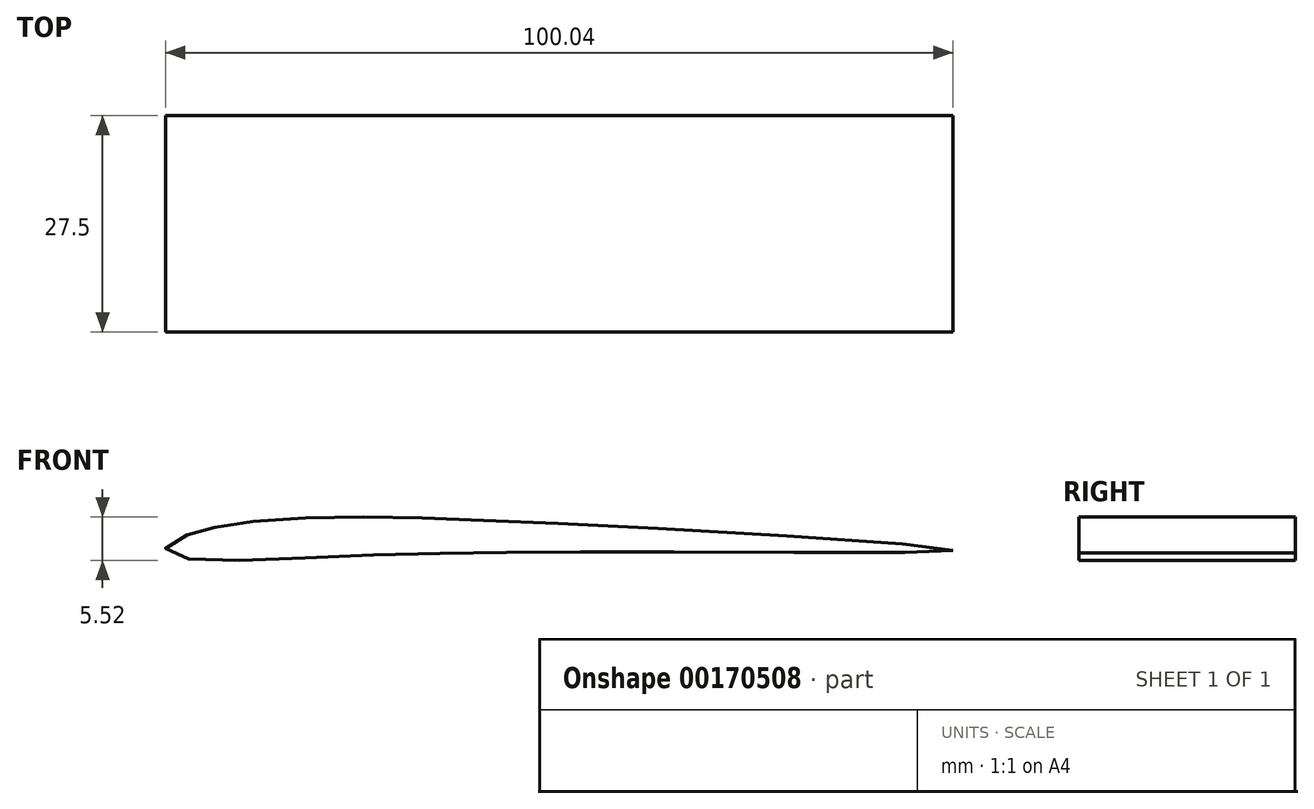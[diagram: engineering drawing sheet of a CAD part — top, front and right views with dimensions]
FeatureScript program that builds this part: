
annotation { "Feature Type Name" : "Feature", "Feature Type Description" : "" }
export const myFeature = defineFeature(function(context is Context, id is Id, definition is map)
    precondition{}
    {
        {
            var Q0;
            Q0=qCreatedBy(makeId("Front.planeOp"),FACE);
            var sketch = newSketch(context, id + "F0", { "sketchPlane" : qUnion([Q0])});
            skFitSpline(sketch, "E0", {"points": [v(50.3, -1.17) * mm, v(12.5, 1.63) * mm, v(-13.6, 2.8) * mm, v(-27.04, 3.06) * mm, v(-38.61, 2.46) * mm, v(-44.14, 1.63) * mm, v(-47.09, 0.77) * mm, v(-49.7, -0.66) * mm, v(-49.07, -1.67) * mm, v(-43.2, -2.45) * mm, v(-26.78, -1.9) * mm, v(-9.56, -1.5) * mm, v(17.45, -1.37) * mm, v(50.3, -1.17) * mm]});
            skSolve(sketch);
        }
        {
            var Q0;
            Q0=makeQuery(id+"F0.imprint","IMPRINT",FACE,{"disambiguationData":[TD([[makeQuery(id+"F0.imprint","IMPRINT",EDGE,{"derivedFrom":sQuery(id+"F0.wireOp",EDGE,"E0")}),1.0]])]});
            var Q1;
            Q1=sQuery(id+"F0.wireOp",EDGE,"E0");
            extrude(context, id + "F1", {"entities" : qUnion([Q0]), "surfaceEntities" : qUnion([Q1]), "depth" : 20 * mm});
        }
        {
            var Q0;
            Q0 = qSketchRegion(id + "F0", true);
            extrude(context, id + "F2", {"entities" : qUnion([Q0]), "operationType" : NewBodyOperationType.ADD, "oppositeDirection" : true, "depth" : 7.5 * mm});
        }
    });
